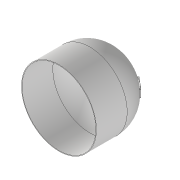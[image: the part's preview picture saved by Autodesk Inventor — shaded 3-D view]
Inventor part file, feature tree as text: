
AUTODESK INVENTOR PART (.ipt)
format: ipt  version: 2020 (Build 240168000, 168)  size: 195,072 bytes
history: native  units: mm
features: sketch x4, extrude x3, revolve x1, projected_geometry x1
ambient origin geometry x8: Origin, YZ Plane, XZ Plane, XY Plane, X Axis, Y Axis, Z Axis, Center Point
bodies: Volumenkörper1 (feature_tree)
feature tree (9):
  revolve  "Umdrehung1"
  extrude  "Extrusion1"  Depth=600.0mm
  extrude  "Extrusion2"  Depth=50.0mm
  extrude  "Extrusion3"  Depth=5.0mm
  sketch  "Skizze1"  dims[d0=0.0mm d1=600.0mm]
  sketch  "Skizze2"  dims[d2=50.0mm d3=500.0mm]
  projected_geometry  "Projizierte Kontur1"
  sketch  "Skizze3"  dims[d4=5.0mm d5=5.0mm]
  sketch  "Skizze4"  dims[d6=50.0mm d7=90.0deg d8=90.0mm d9=10.0mm d10=0.0mm d12=110.0mm d13=27.75mm d14=0.0mm d15=100.0mm d16=0.0mm d17=0.0mm]
